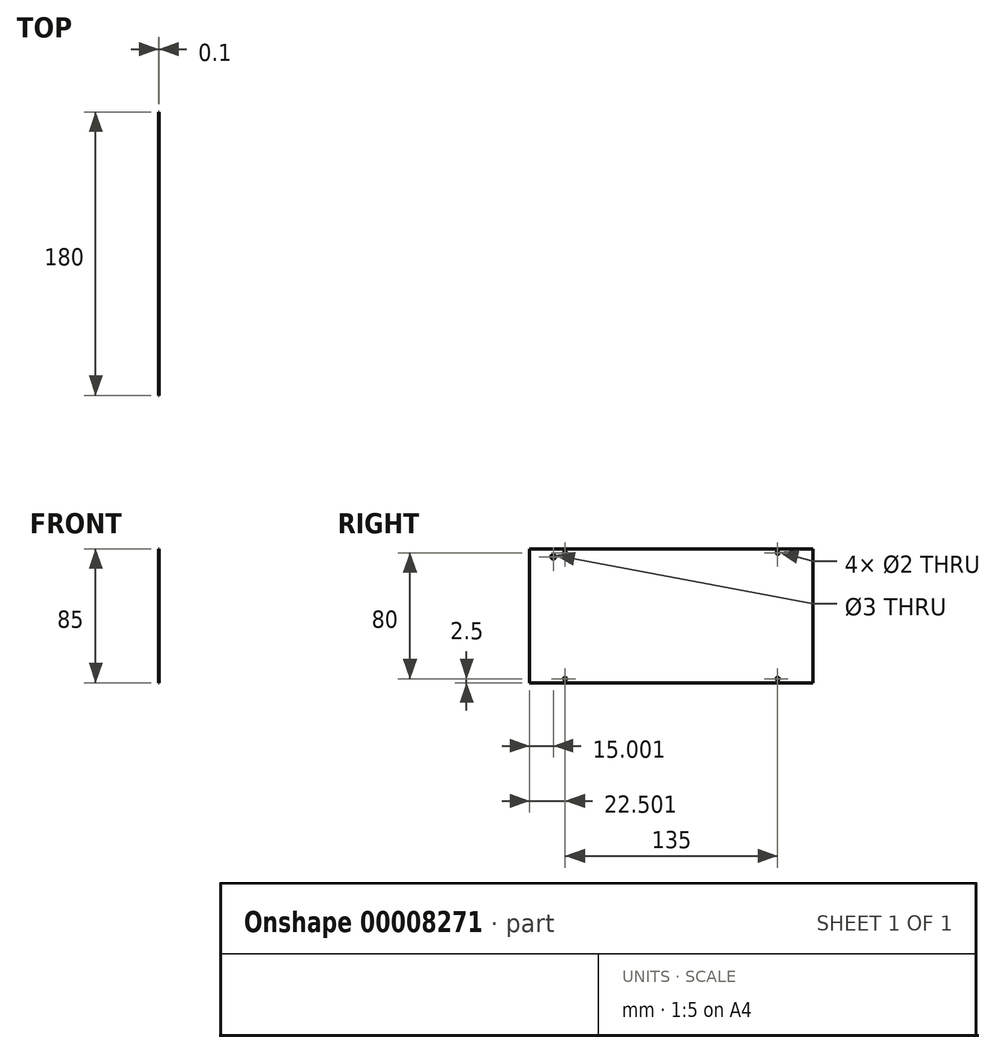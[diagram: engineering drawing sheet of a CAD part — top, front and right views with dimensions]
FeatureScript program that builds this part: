
annotation { "Feature Type Name" : "Feature", "Feature Type Description" : "" }
export const myFeature = defineFeature(function(context is Context, id is Id, definition is map)
    precondition{}
    {
        {
            var Q0;
            Q0=qCreatedBy(makeId("Right.planeOp"),FACE);
            var sketch = newSketch(context, id + "F0", { "sketchPlane" : qUnion([Q0])});
            skLineSegment(sketch, "E0.bottom", {"start": v(-71.1, 34.4) * mm, "end": v(108.9, 34.4) * mm});
            skLineSegment(sketch, "E0.top", {"start": v(-71.1, -50.6) * mm, "end": v(108.9, -50.6) * mm});
            skLineSegment(sketch, "E0.left", {"start": v(-71.1, 34.4) * mm, "end": v(-71.1, -50.6) * mm});
            skLineSegment(sketch, "E0.right", {"start": v(108.9, 34.4) * mm, "end": v(108.9, -50.6) * mm});
            skCircle(sketch, "E1", {"center": v(-48.6, 31.9) * mm, "radius": 1 * mm});
            skPoint(sketch, "E2", {"position": v(18.9, 34.4) * mm});
            skLineSegment(sketch, "E3", {"start": v(18.9, 34.4) * mm, "end": v(18.9, -50.6) * mm, "construction": true});
            skLineSegment(sketch, "E4", {"start": v(18.9, -50.6) * mm, "end": v(18.9, -8.1) * mm, "construction": true});
            skLineSegment(sketch, "E5", {"start": v(108.9, -8.1) * mm, "end": v(-71.1, -8.1) * mm, "construction": true});
            skCircle(sketch, "E6.0.MirrorC", {"center": v(86.4, 31.9) * mm, "radius": 1 * mm});
            skCircle(sketch, "E7.0.MirrorC", {"center": v(86.4, -48.1) * mm, "radius": 1 * mm});
            skCircle(sketch, "E8.0.MirrorC", {"center": v(-48.6, -48.1) * mm, "radius": 1 * mm});
            skCircle(sketch, "E9", {"center": v(-56.1, 29.4) * mm, "radius": 1.5 * mm});
            skSolve(sketch);
        }
        {
            var Q0;
            Q0=qSketchRegion(id+"F0",true);
            extrude(context, id + "F1", {"entities" : qUnion([Q0]), "depth" : 0.1 * mm});
        }
    });
